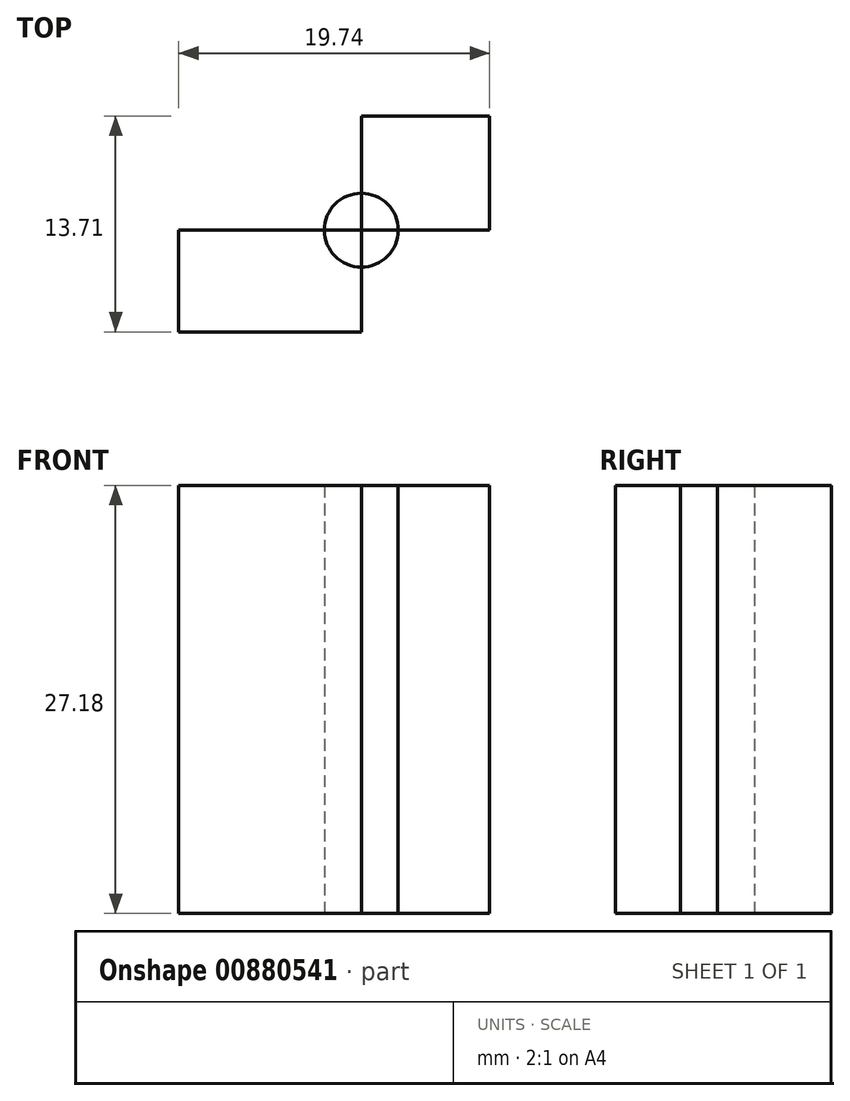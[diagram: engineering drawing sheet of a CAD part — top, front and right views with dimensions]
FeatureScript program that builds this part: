
annotation { "Feature Type Name" : "Feature", "Feature Type Description" : "" }
export const myFeature = defineFeature(function(context is Context, id is Id, definition is map)
    precondition{}
    {
        {
            var Q0;
            Q0=qCreatedBy(makeId("Top.planeOp"),FACE);
            var sketch = newSketch(context, id + "F0", { "sketchPlane" : qUnion([Q0])});
            skLineSegment(sketch, "E0.bottom", {"start": v(-9.06, -7.56) * mm, "end": v(2.53, -7.56) * mm});
            skLineSegment(sketch, "E0.top", {"start": v(-9.06, -14.03) * mm, "end": v(2.53, -14.03) * mm});
            skLineSegment(sketch, "E0.left", {"start": v(-9.06, -7.56) * mm, "end": v(-9.06, -14.03) * mm});
            skLineSegment(sketch, "E0.right", {"start": v(2.53, -7.56) * mm, "end": v(2.53, -14.03) * mm});
            skLineSegment(sketch, "E1.bottom", {"start": v(2.53, -7.56) * mm, "end": v(10.68, -7.56) * mm});
            skLineSegment(sketch, "E1.top", {"start": v(2.53, -0.32) * mm, "end": v(10.68, -0.32) * mm});
            skLineSegment(sketch, "E1.left", {"start": v(2.53, -7.56) * mm, "end": v(2.53, -0.32) * mm});
            skLineSegment(sketch, "E1.right", {"start": v(10.68, -7.56) * mm, "end": v(10.68, -0.32) * mm});
            skCircle(sketch, "E2", {"center": v(2.53, -7.56) * mm, "radius": 2.35 * mm});
            skSolve(sketch);
        }
        {
            var Q0;
            {var subQ2=sQuery(id+"F0.wireOp",EDGE,"E1.top");Q0=makeQuery(id+"F0.imprint","IMPRINT",FACE,{"disambiguationData":[TD([[makeQuery(id+"F0.imprint","IMPRINT",EDGE,{"derivedFrom":subQ2}),-1.0]])]});}
            var Q1;
            {var subQ6=sQuery(id+"F0.wireOp",EDGE,"E0.top");Q1=makeQuery(id+"F0.imprint","IMPRINT",FACE,{"disambiguationData":[TD([[makeQuery(id+"F0.imprint","IMPRINT",EDGE,{"derivedFrom":subQ6}),1.0]])]});}
            var Q2;
            {var subQ1=sQuery(id+"F0.wireOp",EDGE,"E0.right");var subQ3=sQuery(id+"F0.wireOp",EDGE,"E2");var subQ4=makeQuery(id+"F0.imprint","INTERSECT",VERTEX,{"derivedFrom":[subQ1,subQ3]});Q2=makeQuery(id+"F0.imprint","IMPRINT",FACE,{"disambiguationData":[TD([[makeQuery(id+"F0.imprint","IMPRINT",EDGE,{"disambiguationData":[TD([[subQ4,-1.0]])],"derivedFrom":subQ3}),1.0]])]});}
            var Q3;
            {var subQ1=sQuery(id+"F0.wireOp",EDGE,"E0.bottom");var subQ3=sQuery(id+"F0.wireOp",EDGE,"E2");var subQ4=makeQuery(id+"F0.imprint","INTERSECT",VERTEX,{"derivedFrom":[subQ1,subQ3]});Q3=makeQuery(id+"F0.imprint","IMPRINT",FACE,{"disambiguationData":[TD([[makeQuery(id+"F0.imprint","IMPRINT",EDGE,{"disambiguationData":[TD([[subQ4,1.0]])],"derivedFrom":subQ3}),1.0]])]});}
            extrude(context, id + "F1", {"entities" : qUnion([Q0, Q1, Q2, Q3]), "depth" : 27.18 * mm, "offsetDistance" : 25.4 * mm});
        }
    });
